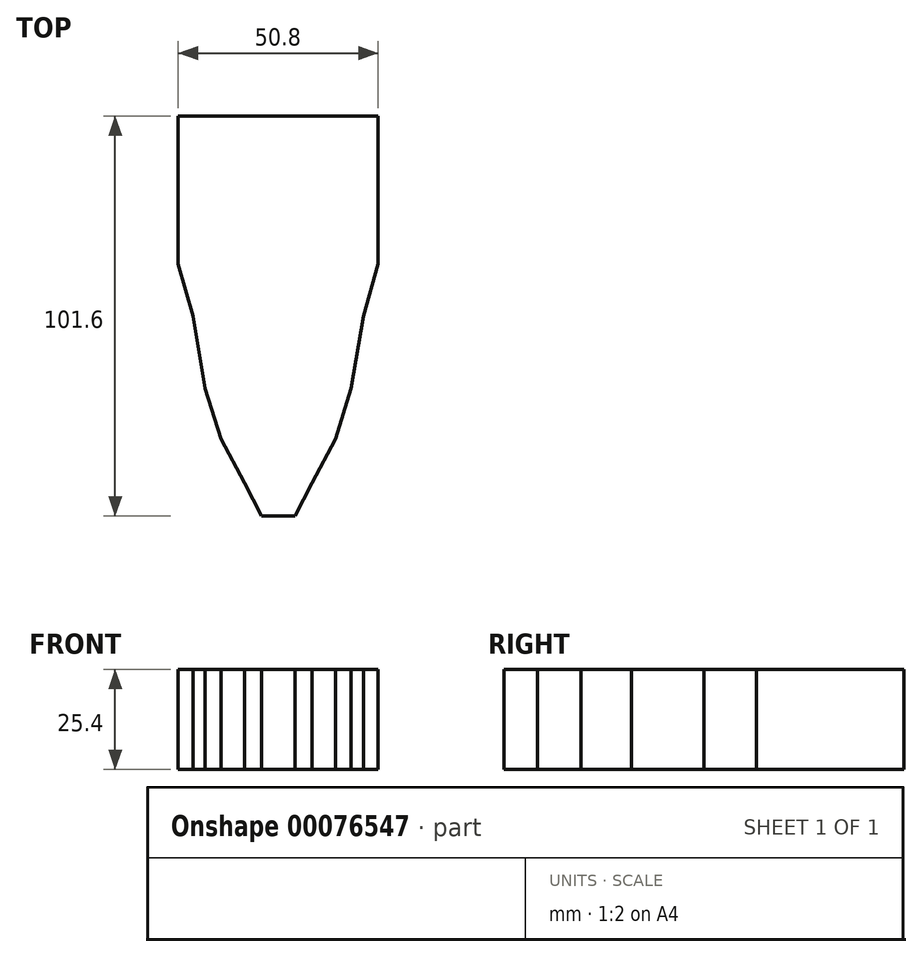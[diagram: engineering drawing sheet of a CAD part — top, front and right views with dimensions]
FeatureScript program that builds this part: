
annotation { "Feature Type Name" : "Feature", "Feature Type Description" : "" }
export const myFeature = defineFeature(function(context is Context, id is Id, definition is map)
    precondition{}
    {
        {
            var Q0;
            Q0=qCreatedBy(makeId("Top.planeOp"),FACE);
            var sketch = newSketch(context, id + "F0", { "sketchPlane" : qUnion([Q0])});
            skLineSegment(sketch, "E0.bottom", {"start": v(25.4, 50.8) * mm, "end": v(-25.4, 50.8) * mm});
            skPoint(sketch, "E0.middle", {"position": v(0, 0) * mm});
            skLineSegment(sketch, "E1", {"start": v(-25.4, 13.26) * mm, "end": v(-21.68, 0) * mm});
            skLineSegment(sketch, "E2", {"start": v(-21.68, 0) * mm, "end": v(-18.54, -18.4) * mm});
            skLineSegment(sketch, "E3", {"start": v(-18.54, -18.4) * mm, "end": v(-14.55, -31.23) * mm});
            skLineSegment(sketch, "E4", {"start": v(-14.55, -31.23) * mm, "end": v(-8.56, -42.36) * mm});
            skLineSegment(sketch, "E5", {"start": v(-8.56, -42.36) * mm, "end": v(-4.28, -50.8) * mm});
            skLineSegment(sketch, "E6", {"start": v(-4.28, -50.8) * mm, "end": v(0, -50.8) * mm});
            skLineSegment(sketch, "E7", {"start": v(0, 50.8) * mm, "end": v(0, -50.8) * mm, "construction": true});
            skLineSegment(sketch, "E8.MirrorCS", {"start": v(25.4, 13.26) * mm, "end": v(21.68, 0) * mm});
            skLineSegment(sketch, "E9.MirrorCS", {"start": v(21.68, 0) * mm, "end": v(18.54, -18.4) * mm});
            skLineSegment(sketch, "E10.MirrorCS", {"start": v(18.54, -18.4) * mm, "end": v(14.55, -31.23) * mm});
            skLineSegment(sketch, "E11.MirrorCS", {"start": v(14.55, -31.23) * mm, "end": v(8.56, -42.36) * mm});
            skLineSegment(sketch, "E12.MirrorCS", {"start": v(8.56, -42.36) * mm, "end": v(4.28, -50.8) * mm});
            skLineSegment(sketch, "E13", {"start": v(4.28, -50.8) * mm, "end": v(-4.28, -50.8) * mm});
            skPoint(sketch, "E14", {"position": v(-25.4, 13.26) * mm});
            skPoint(sketch, "E15", {"position": v(25.4, 13.26) * mm});
            skLineSegment(sketch, "E16", {"start": v(-25.4, 50.8) * mm, "end": v(-25.4, 13.26) * mm});
            skLineSegment(sketch, "E17", {"start": v(25.4, 50.8) * mm, "end": v(25.4, 13.26) * mm});
            skSolve(sketch);
        }
        {
            var Q0;
            Q0 = qSketchRegion(id + "F0", true);
            extrude(context, id + "F1", {"entities" : qUnion([Q0]), "depth" : 25.4 * mm});
        }
    });
